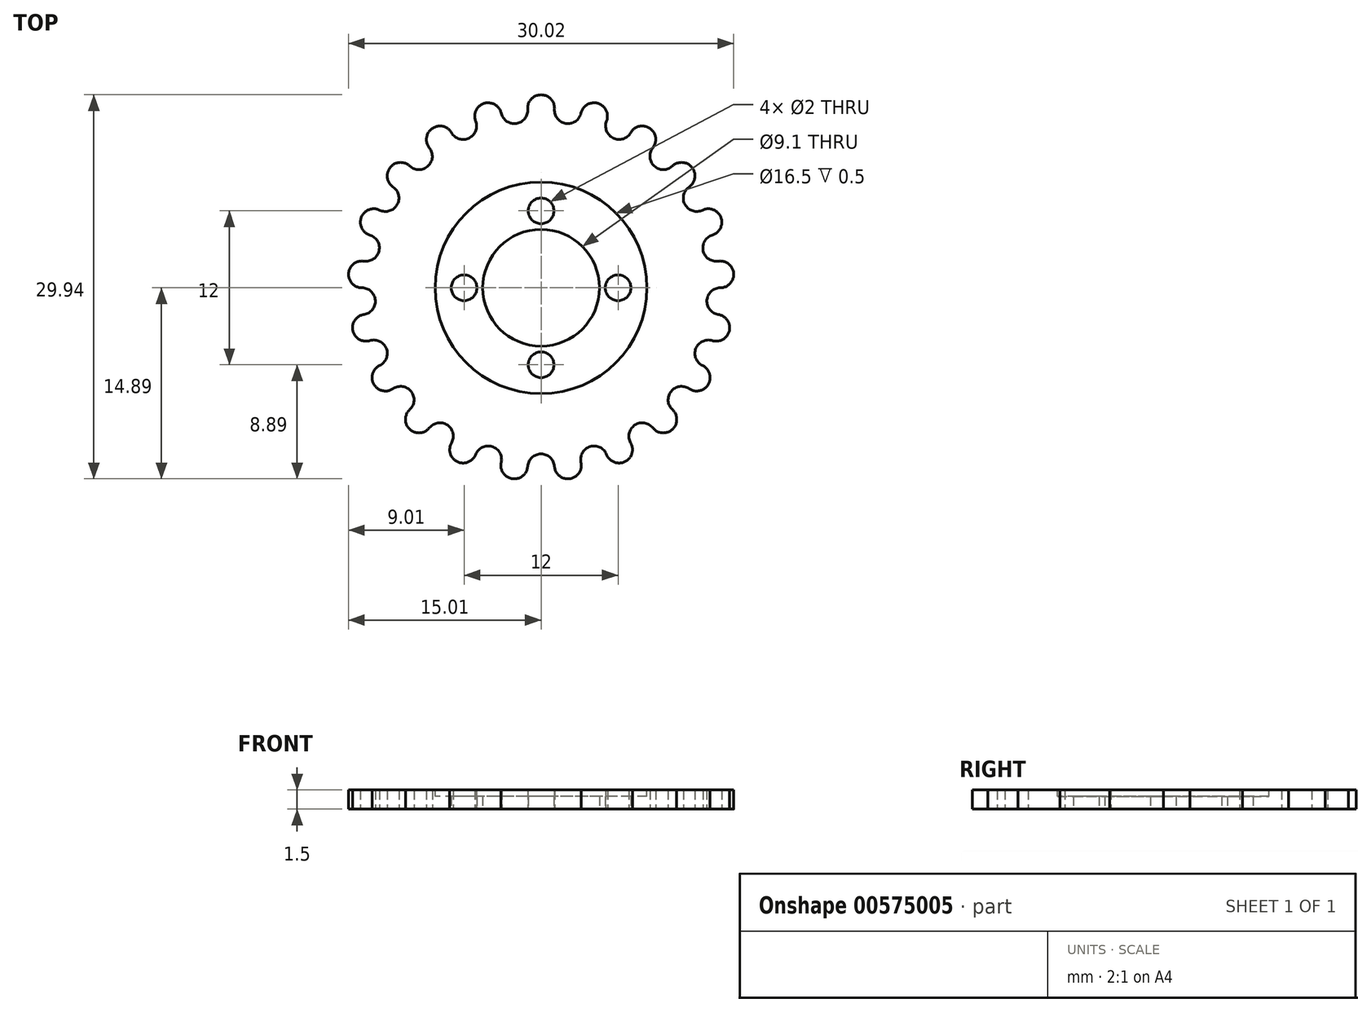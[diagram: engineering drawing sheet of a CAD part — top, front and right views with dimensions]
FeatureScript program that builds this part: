
annotation { "Feature Type Name" : "Feature", "Feature Type Description" : "" }
export const myFeature = defineFeature(function(context is Context, id is Id, definition is map)
    precondition{}
    {
        {
            var Q0;
            Q0=qCreatedBy(makeId("Top.planeOp"),FACE);
            var sketch = newSketch(context, id + "F0", { "sketchPlane" : qUnion([Q0])});
            skCircle(sketch, "E0", {"center": v(0, 0) * mm, "radius": 4.55 * mm});
            skCircle(sketch, "E1", {"center": v(0, 6) * mm, "radius": 1 * mm});
            skCircle(sketch, "E2.1.0", {"center": v(-6, 0) * mm, "radius": 1 * mm});
            skCircle(sketch, "E2.2.0", {"center": v(0, -6) * mm, "radius": 1 * mm});
            skCircle(sketch, "E3.1.3.0", {"center": v(6, 0) * mm, "radius": 1 * mm});
            skArc(sketch, "E4", {"start": v(1.04, 13.92) * mm, "mid": v(0, 15.05) * mm, "end": v(-1.04, 13.92) * mm});
            skArc(sketch, "E5.1.0", {"start": v(-3.1, 13.61) * mm, "mid": v(-1.93, 12.8) * mm, "end": v(-1.04, 13.92) * mm});
            skArc(sketch, "E5.2.0", {"start": v(-3.1, 13.61) * mm, "mid": v(-4.43, 14.38) * mm, "end": v(-5.1, 13) * mm});
            skArc(sketch, "E6.1.3.0", {"start": v(-6.98, 12.1) * mm, "mid": v(-5.62, 11.67) * mm, "end": v(-5.1, 13) * mm});
            skArc(sketch, "E6.1.4.0", {"start": v(-6.98, 12.1) * mm, "mid": v(-8.48, 12.43) * mm, "end": v(-8.7, 10.92) * mm});
            skArc(sketch, "E6.1.5.0", {"start": v(-10.23, 9.5) * mm, "mid": v(-8.81, 9.5) * mm, "end": v(-8.7, 10.92) * mm});
            skArc(sketch, "E6.1.6.0", {"start": v(-10.23, 9.5) * mm, "mid": v(-11.76, 9.38) * mm, "end": v(-11.53, 7.86) * mm});
            skArc(sketch, "E6.1.7.0", {"start": v(-12.58, 6.06) * mm, "mid": v(-11.22, 6.48) * mm, "end": v(-11.53, 7.86) * mm});
            skArc(sketch, "E6.1.8.0", {"start": v(-12.58, 6.06) * mm, "mid": v(-14, 5.5) * mm, "end": v(-13.34, 4.12) * mm});
            skArc(sketch, "E6.1.9.0", {"start": v(-13.8, 2.08) * mm, "mid": v(-12.63, 2.88) * mm, "end": v(-13.34, 4.12) * mm});
            skArc(sketch, "E6.1.10.0", {"start": v(-13.8, 2.08) * mm, "mid": v(-15, 1.12) * mm, "end": v(-13.96, 0) * mm});
            skArc(sketch, "E6.1.11.0", {"start": v(-13.8, -2.08) * mm, "mid": v(-12.92, -0.97) * mm, "end": v(-13.96, 0) * mm});
            skArc(sketch, "E6.1.12.0", {"start": v(-13.8, -2.08) * mm, "mid": v(-14.67, -3.35) * mm, "end": v(-13.34, -4.12) * mm});
            skArc(sketch, "E6.1.13.0", {"start": v(-12.58, -6.06) * mm, "mid": v(-12.06, -4.73) * mm, "end": v(-13.34, -4.12) * mm});
            skArc(sketch, "E6.1.14.0", {"start": v(-12.58, -6.06) * mm, "mid": v(-13.03, -7.52) * mm, "end": v(-11.53, -7.86) * mm});
            skArc(sketch, "E6.1.15.0", {"start": v(-10.23, -9.5) * mm, "mid": v(-10.13, -8.08) * mm, "end": v(-11.53, -7.86) * mm});
            skArc(sketch, "E6.1.16.0", {"start": v(-10.23, -9.5) * mm, "mid": v(-10.23, -11.03) * mm, "end": v(-8.7, -10.92) * mm});
            skArc(sketch, "E6.1.17.0", {"start": v(-6.98, -12.1) * mm, "mid": v(-7.3, -10.7) * mm, "end": v(-8.7, -10.92) * mm});
            skArc(sketch, "E6.1.18.0", {"start": v(-6.98, -12.1) * mm, "mid": v(-6.53, -13.56) * mm, "end": v(-5.1, -13) * mm});
            skArc(sketch, "E6.1.19.0", {"start": v(-3.1, -13.61) * mm, "mid": v(-3.82, -12.38) * mm, "end": v(-5.1, -13) * mm});
            skArc(sketch, "E6.1.20.0", {"start": v(-3.1, -13.61) * mm, "mid": v(-2.24, -14.88) * mm, "end": v(-1.04, -13.92) * mm});
            skArc(sketch, "E6.1.21.0", {"start": v(1.04, -13.92) * mm, "mid": v(0, -12.95) * mm, "end": v(-1.04, -13.92) * mm});
            skArc(sketch, "E7.1.22.0", {"start": v(1.04, -13.92) * mm, "mid": v(2.24, -14.88) * mm, "end": v(3.1, -13.61) * mm});
            skArc(sketch, "E7.1.23.0", {"start": v(5.1, -13) * mm, "mid": v(3.82, -12.38) * mm, "end": v(3.1, -13.61) * mm});
            skArc(sketch, "E7.1.24.0", {"start": v(5.1, -13) * mm, "mid": v(6.53, -13.56) * mm, "end": v(6.98, -12.1) * mm});
            skArc(sketch, "E7.1.25.0", {"start": v(8.7, -10.92) * mm, "mid": v(7.3, -10.7) * mm, "end": v(6.98, -12.1) * mm});
            skArc(sketch, "E7.1.26.0", {"start": v(8.7, -10.92) * mm, "mid": v(10.23, -11.03) * mm, "end": v(10.23, -9.5) * mm});
            skArc(sketch, "E7.1.27.0", {"start": v(11.53, -7.86) * mm, "mid": v(10.13, -8.08) * mm, "end": v(10.23, -9.5) * mm});
            skArc(sketch, "E7.1.28.0", {"start": v(11.53, -7.86) * mm, "mid": v(13.03, -7.52) * mm, "end": v(12.58, -6.06) * mm});
            skArc(sketch, "E7.1.29.0", {"start": v(13.34, -4.12) * mm, "mid": v(12.06, -4.73) * mm, "end": v(12.58, -6.06) * mm});
            skArc(sketch, "E8.1.30.0", {"start": v(13.34, -4.12) * mm, "mid": v(14.67, -3.35) * mm, "end": v(13.8, -2.08) * mm});
            skArc(sketch, "E8.1.31.0", {"start": v(13.96, 0) * mm, "mid": v(12.92, -0.97) * mm, "end": v(13.8, -2.08) * mm});
            skArc(sketch, "E9.1.32.0", {"start": v(13.96, 0) * mm, "mid": v(15, 1.12) * mm, "end": v(13.8, 2.08) * mm});
            skArc(sketch, "E9.1.33.0", {"start": v(13.34, 4.12) * mm, "mid": v(12.63, 2.88) * mm, "end": v(13.8, 2.08) * mm});
            skArc(sketch, "E9.1.34.0", {"start": v(13.34, 4.12) * mm, "mid": v(14, 5.5) * mm, "end": v(12.58, 6.06) * mm});
            skArc(sketch, "E9.1.35.0", {"start": v(11.53, 7.86) * mm, "mid": v(11.22, 6.48) * mm, "end": v(12.58, 6.06) * mm});
            skArc(sketch, "E10.1.36.0", {"start": v(11.53, 7.86) * mm, "mid": v(11.76, 9.38) * mm, "end": v(10.23, 9.5) * mm});
            skArc(sketch, "E10.1.37.0", {"start": v(8.7, 10.92) * mm, "mid": v(8.81, 9.5) * mm, "end": v(10.23, 9.5) * mm});
            skArc(sketch, "E11.1.38.0", {"start": v(8.7, 10.92) * mm, "mid": v(8.48, 12.43) * mm, "end": v(6.98, 12.1) * mm});
            skArc(sketch, "E11.1.39.0", {"start": v(5.1, 13) * mm, "mid": v(5.62, 11.67) * mm, "end": v(6.98, 12.1) * mm});
            skArc(sketch, "E12.1.40.0", {"start": v(5.1, 13) * mm, "mid": v(4.43, 14.38) * mm, "end": v(3.1, 13.61) * mm});
            skArc(sketch, "E12.1.41.0", {"start": v(1.04, 13.92) * mm, "mid": v(1.93, 12.8) * mm, "end": v(3.1, 13.61) * mm});
            skSolve(sketch);
        }
        {
            var Q0;
            Q0 = qSketchRegion(id + "F0", true);
            extrude(context, id + "F1", {"entities" : qUnion([Q0]), "depth" : 1.5 * mm, "offsetDistance" : 25 * mm});
        }
        {
            var Q0;
            Q0=makeQuery(id+"F1.opExtrude","CAP_FACE",FACE,{"disambiguationData":[OSD([sQuery(id+"F0.wireOp",EDGE,"E0"),sQuery(id+"F0.wireOp",EDGE,"E1"),sQuery(id+"F0.wireOp",EDGE,"E2.1.0"),sQuery(id+"F0.wireOp",EDGE,"E2.2.0"),sQuery(id+"F0.wireOp",EDGE,"E3.1.3.0"),sQuery(id+"F0.wireOp",EDGE,"E4"),sQuery(id+"F0.wireOp",EDGE,"E5.1.0"),sQuery(id+"F0.wireOp",EDGE,"E5.2.0"),sQuery(id+"F0.wireOp",EDGE,"E6.1.3.0"),sQuery(id+"F0.wireOp",EDGE,"E6.1.4.0"),sQuery(id+"F0.wireOp",EDGE,"E6.1.5.0"),sQuery(id+"F0.wireOp",EDGE,"E6.1.6.0"),sQuery(id+"F0.wireOp",EDGE,"E6.1.7.0"),sQuery(id+"F0.wireOp",EDGE,"E6.1.8.0"),sQuery(id+"F0.wireOp",EDGE,"E6.1.9.0"),sQuery(id+"F0.wireOp",EDGE,"E6.1.10.0"),sQuery(id+"F0.wireOp",EDGE,"E6.1.11.0"),sQuery(id+"F0.wireOp",EDGE,"E6.1.12.0"),sQuery(id+"F0.wireOp",EDGE,"E6.1.13.0"),sQuery(id+"F0.wireOp",EDGE,"E6.1.14.0"),sQuery(id+"F0.wireOp",EDGE,"E6.1.15.0"),sQuery(id+"F0.wireOp",EDGE,"E6.1.16.0"),sQuery(id+"F0.wireOp",EDGE,"E6.1.17.0"),sQuery(id+"F0.wireOp",EDGE,"E6.1.18.0"),sQuery(id+"F0.wireOp",EDGE,"E6.1.19.0"),sQuery(id+"F0.wireOp",EDGE,"E6.1.20.0"),sQuery(id+"F0.wireOp",EDGE,"E6.1.21.0"),sQuery(id+"F0.wireOp",EDGE,"E7.1.22.0"),sQuery(id+"F0.wireOp",EDGE,"E7.1.23.0"),sQuery(id+"F0.wireOp",EDGE,"E7.1.24.0"),sQuery(id+"F0.wireOp",EDGE,"E7.1.25.0"),sQuery(id+"F0.wireOp",EDGE,"E7.1.26.0"),sQuery(id+"F0.wireOp",EDGE,"E7.1.27.0"),sQuery(id+"F0.wireOp",EDGE,"E7.1.28.0"),sQuery(id+"F0.wireOp",EDGE,"E7.1.29.0"),sQuery(id+"F0.wireOp",EDGE,"E8.1.30.0"),sQuery(id+"F0.wireOp",EDGE,"E8.1.31.0"),sQuery(id+"F0.wireOp",EDGE,"E9.1.32.0"),sQuery(id+"F0.wireOp",EDGE,"E9.1.33.0"),sQuery(id+"F0.wireOp",EDGE,"E9.1.34.0"),sQuery(id+"F0.wireOp",EDGE,"E9.1.35.0"),sQuery(id+"F0.wireOp",EDGE,"E10.1.36.0"),sQuery(id+"F0.wireOp",EDGE,"E10.1.37.0"),sQuery(id+"F0.wireOp",EDGE,"E11.1.38.0"),sQuery(id+"F0.wireOp",EDGE,"E11.1.39.0"),sQuery(id+"F0.wireOp",EDGE,"E12.1.40.0"),sQuery(id+"F0.wireOp",EDGE,"E12.1.41.0")])],"isStart":false});
            var sketch = newSketch(context, id + "F2", { "sketchPlane" : qUnion([Q0])});
            skCircle(sketch, "E13", {"center": v(0, 0) * mm, "radius": 8.25 * mm});
            skSolve(sketch);
        }
        {
            var Q0;
            Q0 = qSketchRegion(id + "F2", true);
            extrude(context, id + "F3", {"entities" : qUnion([Q0]), "operationType" : NewBodyOperationType.REMOVE, "oppositeDirection" : true, "depth" : 0.5 * mm, "offsetDistance" : 25 * mm});
        }
    });
